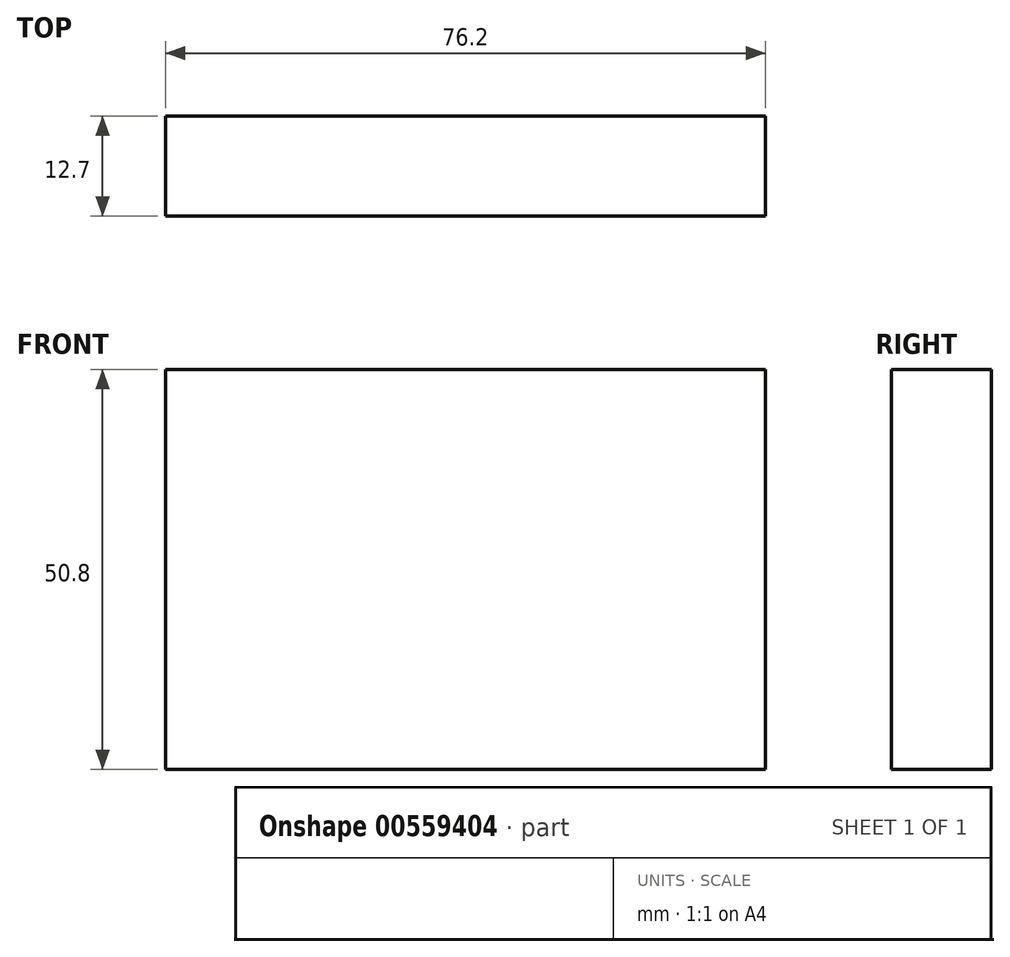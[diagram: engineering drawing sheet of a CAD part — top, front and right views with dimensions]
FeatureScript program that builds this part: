
annotation { "Feature Type Name" : "Feature", "Feature Type Description" : "" }
export const myFeature = defineFeature(function(context is Context, id is Id, definition is map)
    precondition{}
    {
        {
            var Q0;
            Q0=qCreatedBy(makeId("Front.planeOp"),FACE);
            var sketch = newSketch(context, id + "F0", { "sketchPlane" : qUnion([Q0])});
            skLineSegment(sketch, "E0.bottom", {"start": v(40.05, -25.4) * mm, "end": v(-36.15, -25.4) * mm});
            skLineSegment(sketch, "E0.top", {"start": v(40.05, 25.4) * mm, "end": v(-36.15, 25.4) * mm});
            skLineSegment(sketch, "E0.left", {"start": v(40.05, -25.4) * mm, "end": v(40.05, 25.4) * mm});
            skLineSegment(sketch, "E0.right", {"start": v(-36.15, -25.4) * mm, "end": v(-36.15, 25.4) * mm});
            skPoint(sketch, "E0.middle", {"position": v(1.95, 0) * mm});
            skSolve(sketch);
        }
        {
            var Q0;
            Q0 = qSketchRegion(id + "F0", true);
            extrude(context, id + "F1", {"entities" : qUnion([Q0]), "depth" : 12.7 * mm, "offsetDistance" : 25.4 * mm});
        }
    });
